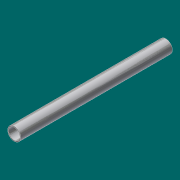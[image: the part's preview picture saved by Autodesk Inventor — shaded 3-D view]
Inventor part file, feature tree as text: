
AUTODESK INVENTOR PART (.ipt)
format: ipt  version: 2017 (Build 210142000, 142)  size: 114,688 bytes
history: native  units: in
note: dims shown in document units (in); Inventor stores cm internally (conversion verified against a paired STEP export)
features: extrude x1, sketch x1
ambient origin geometry x8: Origin, YZ Plane, XZ Plane, XY Plane, X Axis, Y Axis, Z Axis, Center Point
bodies: Solid1 (feature_tree)
feature tree (2):
  extrude  "Extrusion1"  Depth=33.25in
  sketch  "Sketch1"  dims[d0=2.875in d1=2.469in d2=33.25in d3=0.0in]
